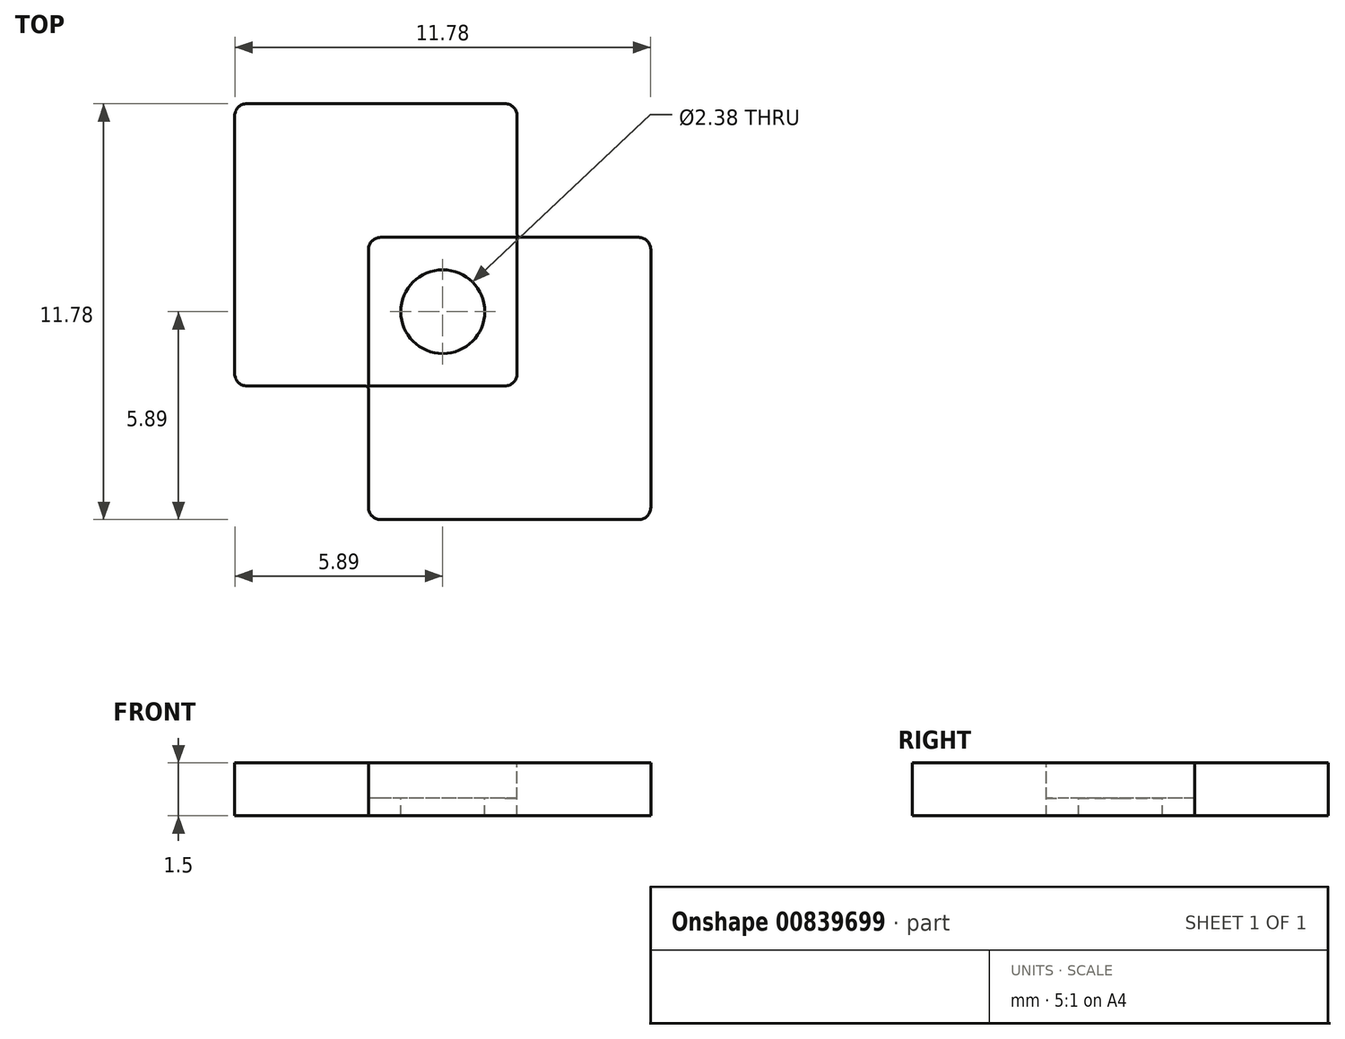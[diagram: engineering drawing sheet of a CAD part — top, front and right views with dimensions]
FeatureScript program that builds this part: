
annotation { "Feature Type Name" : "Feature", "Feature Type Description" : "" }
export const myFeature = defineFeature(function(context is Context, id is Id, definition is map)
    precondition{}
    {
        {
            var Q0;
            Q0=qCreatedBy(makeId("Top.planeOp"),FACE);
            var sketch = newSketch(context, id + "F0", { "sketchPlane" : qUnion([Q0])});
            skLineSegment(sketch, "E0", {"start": v(-5.55, 5.9) * mm, "end": v(1.76, 5.9) * mm});
            skLineSegment(sketch, "E1", {"start": v(2.1, 5.55) * mm, "end": v(2.1, 2.1) * mm});
            skLineSegment(sketch, "E2", {"start": v(2.1, 2.1) * mm, "end": v(-1.76, 2.1) * mm});
            skLineSegment(sketch, "E3", {"start": v(-2.1, 1.76) * mm, "end": v(-2.1, -2.1) * mm});
            skLineSegment(sketch, "E4", {"start": v(-2.1, -2.1) * mm, "end": v(-5.55, -2.1) * mm});
            skLineSegment(sketch, "E5", {"start": v(-5.9, -1.76) * mm, "end": v(-5.9, 5.55) * mm});
            skLineSegment(sketch, "E6", {"start": v(-2.1, -2.1) * mm, "end": v(2.1, 2.1) * mm, "construction": true});
            skArc(sketch, "E7", {"start": v(-0.84, -0.84) * mm, "mid": v(-0.84, 0.84) * mm, "end": v(0.84, 0.84) * mm});
            skPoint(sketch, "E8.visualSharp", {"position": v(-5.9, -2.1) * mm});
            skArc(sketch, "E8.filletArc", {"start": v(-5.9, -1.76) * mm, "mid": v(-5.8, -2) * mm, "end": v(-5.55, -2.1) * mm});
            skPoint(sketch, "E9.visualSharp", {"position": v(-2.1, 2.1) * mm});
            skArc(sketch, "E9.filletArc", {"start": v(-1.76, 2.1) * mm, "mid": v(-2, 2) * mm, "end": v(-2.1, 1.76) * mm});
            skPoint(sketch, "E10.visualSharp", {"position": v(2.1, 5.9) * mm});
            skArc(sketch, "E10.filletArc", {"start": v(2.1, 5.55) * mm, "mid": v(2, 5.8) * mm, "end": v(1.76, 5.9) * mm});
            skPoint(sketch, "E11.visualSharp", {"position": v(-5.9, 5.9) * mm});
            skArc(sketch, "E11.filletArc", {"start": v(-5.55, 5.9) * mm, "mid": v(-5.8, 5.8) * mm, "end": v(-5.9, 5.55) * mm});
            skArc(sketch, "E12.MirrorCS", {"start": v(-0.84, -0.84) * mm, "mid": v(0.84, -0.84) * mm, "end": v(0.84, 0.84) * mm});
            skLineSegment(sketch, "E13.MirrorCS", {"start": v(1.76, -2.1) * mm, "end": v(-2.1, -2.1) * mm});
            skArc(sketch, "E14.MirrorCS", {"start": v(2.1, -1.76) * mm, "mid": v(2, -2) * mm, "end": v(1.76, -2.1) * mm});
            skLineSegment(sketch, "E15.MirrorCS", {"start": v(2.1, 2.1) * mm, "end": v(2.1, -1.76) * mm});
            skLineSegment(sketch, "E16.MirrorCS", {"start": v(5.55, 2.1) * mm, "end": v(2.1, 2.1) * mm});
            skArc(sketch, "E17.MirrorCS", {"start": v(5.55, 2.1) * mm, "mid": v(5.8, 2) * mm, "end": v(5.9, 1.76) * mm});
            skLineSegment(sketch, "E18.MirrorCS", {"start": v(5.9, -5.55) * mm, "end": v(5.9, 1.76) * mm});
            skArc(sketch, "E19.MirrorCS", {"start": v(5.9, -5.55) * mm, "mid": v(5.8, -5.8) * mm, "end": v(5.55, -5.9) * mm});
            skLineSegment(sketch, "E20.MirrorCS", {"start": v(-1.76, -5.9) * mm, "end": v(5.55, -5.9) * mm});
            skArc(sketch, "E21.MirrorCS", {"start": v(-1.76, -5.9) * mm, "mid": v(-2, -5.8) * mm, "end": v(-2.1, -5.55) * mm});
            skLineSegment(sketch, "E22.MirrorCS", {"start": v(-2.1, -2.1) * mm, "end": v(-2.1, -5.55) * mm});
            skSolve(sketch);
        }
        {
            var Q0;
            Q0=makeQuery(id+"F0.imprint","IMPRINT",FACE,{"disambiguationData":[TD([[makeQuery(id+"F0.imprint","IMPRINT",EDGE,{"derivedFrom":sQuery(id+"F0.wireOp",EDGE,"E0")}),-1.0]])]});
            var Q1;
            Q1=makeQuery(id+"F0.imprint","IMPRINT",FACE,{"disambiguationData":[TD([[makeQuery(id+"F0.imprint","IMPRINT",EDGE,{"derivedFrom":sQuery(id+"F0.wireOp",EDGE,"E2")}),1.0]])]});
            var Q2;
            Q2=makeQuery(id+"F0.imprint","IMPRINT",FACE,{"disambiguationData":[TD([[makeQuery(id+"F0.imprint","IMPRINT",EDGE,{"derivedFrom":sQuery(id+"F0.wireOp",EDGE,"E7")}),-1.0]])]});
            var Q3;
            Q3=makeQuery(id+"F0.imprint","IMPRINT",FACE,{"disambiguationData":[TD([[makeQuery(id+"F0.imprint","IMPRINT",EDGE,{"derivedFrom":sQuery(id+"F0.wireOp",EDGE,"E13.MirrorCS")}),1.0]])]});
            extrude(context, id + "F1", {"entities" : qUnion([Q0, Q1, Q2, Q3]), "oppositeDirection" : true, "depth" : 1.5 * mm, "offsetDistance" : 25 * mm});
        }
        {
            var Q0;
            Q0=makeQuery(id+"F1.opExtrude","SWEPT_EDGE",EDGE,{"disambiguationData":[OSD([sQuery(id+"F0.wireOp",EDGE,"E3"),sQuery(id+"F0.wireOp",EDGE,"E4"),sQuery(id+"F0.wireOp",EDGE,"E13.MirrorCS"),sQuery(id+"F0.wireOp",EDGE,"E22.MirrorCS")])]});
            var Q1;
            Q1=makeQuery(id+"F1.opExtrude","SWEPT_EDGE",EDGE,{"disambiguationData":[OSD([sQuery(id+"F0.wireOp",EDGE,"E1"),sQuery(id+"F0.wireOp",EDGE,"E2"),sQuery(id+"F0.wireOp",EDGE,"E15.MirrorCS"),sQuery(id+"F0.wireOp",EDGE,"E16.MirrorCS")])]});
            fillet(context, id + "F2", {"entities" : qUnion([Q0, Q1]), "radius" : 0.1 * mm, "tangentPropagation" : true, "allowEdgeOverflow" : false});
        }
        {
            var Q0;
            Q0=makeQuery(id+"F0.imprint","IMPRINT",FACE,{"disambiguationData":[TD([[makeQuery(id+"F0.imprint","IMPRINT",EDGE,{"derivedFrom":sQuery(id+"F0.wireOp",EDGE,"E2")}),1.0]])]});
            extrude(context, id + "F3", {"entities" : qUnion([Q0]), "operationType" : NewBodyOperationType.REMOVE, "oppositeDirection" : true, "depth" : 1 * mm, "offsetDistance" : 25 * mm});
        }
    });
